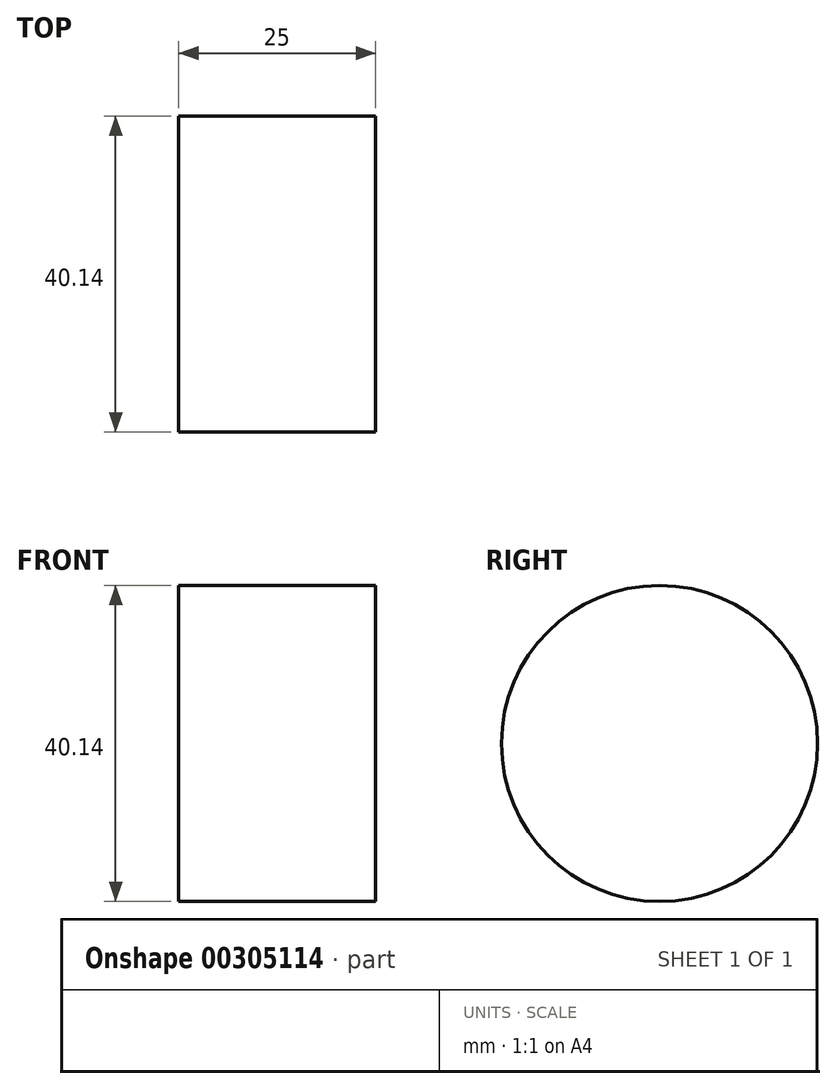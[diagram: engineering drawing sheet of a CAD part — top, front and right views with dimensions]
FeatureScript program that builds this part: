
annotation { "Feature Type Name" : "Feature", "Feature Type Description" : "" }
export const myFeature = defineFeature(function(context is Context, id is Id, definition is map)
    precondition{}
    {
        {
            var Q0;
            Q0=qCreatedBy(makeId("Right.planeOp"),FACE);
            var sketch = newSketch(context, id + "F0", { "sketchPlane" : qUnion([Q0])});
            skCircle(sketch, "E0", {"center": v(0, 0) * mm, "radius": 20.07 * mm});
            skSolve(sketch);
        }
        {
            var Q0;
            Q0=sQuery(id+"F0.wireOp",EDGE,"E0");
            extrude(context, id + "F1", {"bodyType" : ToolBodyType.SURFACE, "surfaceEntities" : qUnion([Q0]), "depth" : 25 * mm});
        }
    });
